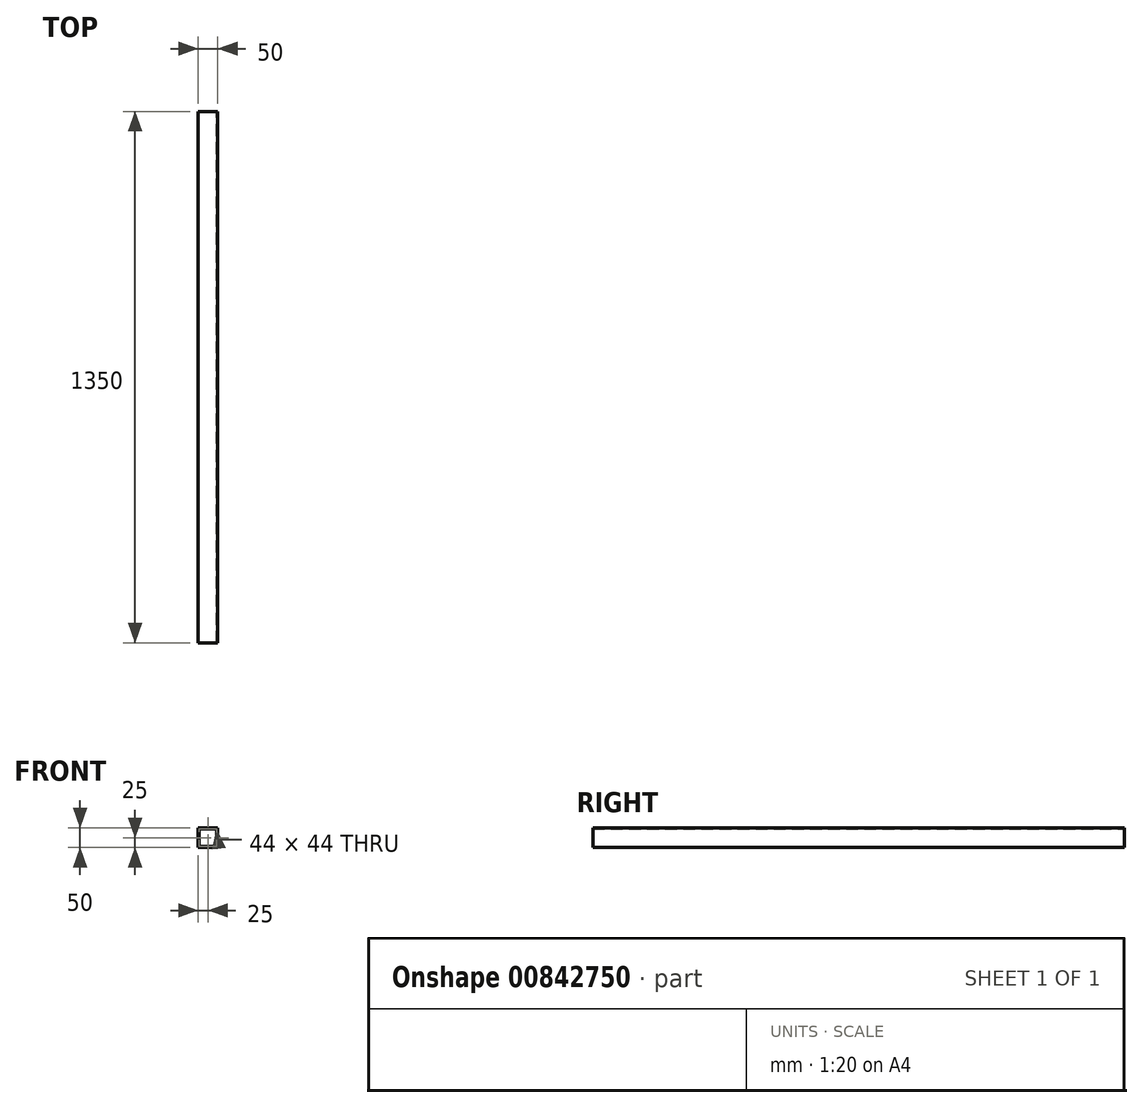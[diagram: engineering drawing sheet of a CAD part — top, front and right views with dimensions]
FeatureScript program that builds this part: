
annotation { "Feature Type Name" : "Feature", "Feature Type Description" : "" }
export const myFeature = defineFeature(function(context is Context, id is Id, definition is map)
    precondition{}
    {
        {
            var Q0;
            Q0=qCreatedBy(makeId("Front.planeOp"),FACE);
            var sketch = newSketch(context, id + "F0", { "sketchPlane" : qUnion([Q0])});
            skLineSegment(sketch, "E0.bottom", {"start": v(25, -25) * mm, "end": v(-25, -25) * mm});
            skLineSegment(sketch, "E0.top", {"start": v(25, 25) * mm, "end": v(-25, 25) * mm});
            skLineSegment(sketch, "E0.left", {"start": v(25, -25) * mm, "end": v(25, 25) * mm});
            skLineSegment(sketch, "E0.right", {"start": v(-25, -25) * mm, "end": v(-25, 25) * mm});
            skPoint(sketch, "E0.middle", {"position": v(0, 0) * mm});
            skLineSegment(sketch, "E1.0", {"start": v(22, 22) * mm, "end": v(-22, 22) * mm});
            skLineSegment(sketch, "E1.1", {"start": v(22, -22) * mm, "end": v(22, 22) * mm});
            skLineSegment(sketch, "E1.2", {"start": v(22, -22) * mm, "end": v(-22, -22) * mm});
            skLineSegment(sketch, "E1.3", {"start": v(-22, -22) * mm, "end": v(-22, 22) * mm});
            skSolve(sketch);
        }
        {
            var Q0;
            Q0=makeQuery(id+"F0.imprint","IMPRINT",FACE,{"disambiguationData":[TD([[makeQuery(id+"F0.imprint","IMPRINT",EDGE,{"derivedFrom":sQuery(id+"F0.wireOp",EDGE,"E0.bottom")}),-1.0]])]});
            extrude(context, id + "F1", {"entities" : qUnion([Q0]), "depth" : 1350 * mm, "offsetDistance" : 25 * mm});
        }
    });
